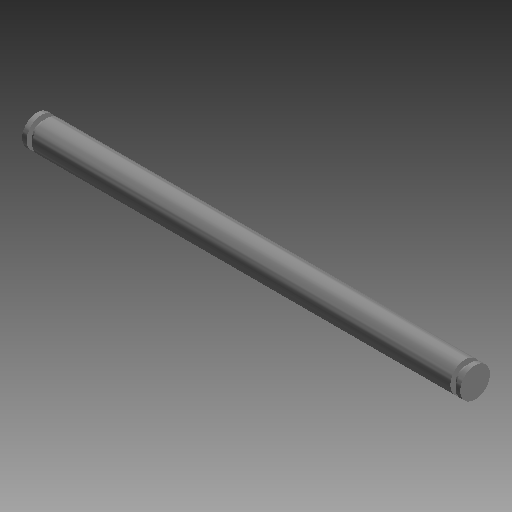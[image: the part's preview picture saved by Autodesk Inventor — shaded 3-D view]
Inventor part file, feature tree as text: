
AUTODESK INVENTOR PART (.ipt)
format: ipt  version: 2019 (Build 230136000, 136)  size: 72,704 bytes
history: native  units: mm (DEFAULTED — no unit token found)
features: revolve x1
ambient origin geometry x8: Origin, YZ Plane, XZ Plane, XY Plane, X Axis, Y Axis, Z Axis, Center Point
bodies: Solid1 (feature_tree)
feature tree (1):
  revolve  "Revolve1"  [1 undecoded]
note: 1 required parameter value undecoded (feature->parameter linkage not recoverable at this tier; creation-order binding heuristic only, values carry confidence <= 0.55)
